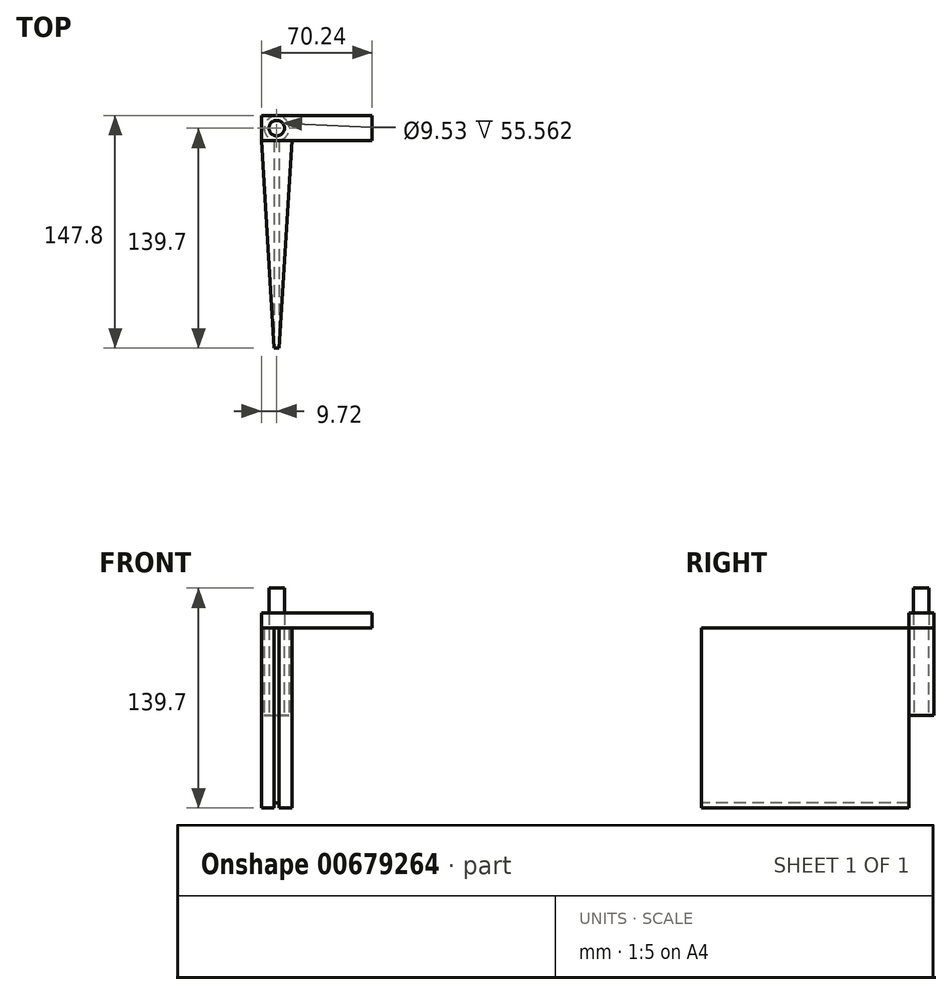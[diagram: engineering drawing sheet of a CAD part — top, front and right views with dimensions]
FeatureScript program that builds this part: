
annotation { "Feature Type Name" : "Feature", "Feature Type Description" : "" }
export const myFeature = defineFeature(function(context is Context, id is Id, definition is map)
    precondition{}
    {
        {
            var Q0;
            Q0=qCreatedBy(makeId("Top.planeOp"),FACE);
            var sketch = newSketch(context, id + "F0", { "sketchPlane" : qUnion([Q0])});
            skCircle(sketch, "E0", {"center": v(0, 0) * mm, "radius": 7.94 * mm});
            skCircle(sketch, "E1", {"center": v(0, 0) * mm, "radius": 4.76 * mm});
            skLineSegment(sketch, "E2.top", {"start": v(1.59, -139.7) * mm, "end": v(-1.59, -139.7) * mm});
            skLineSegment(sketch, "E2.left", {"start": v(1.59, 0) * mm, "end": v(1.59, -139.7) * mm});
            skLineSegment(sketch, "E2.right", {"start": v(-1.59, 0) * mm, "end": v(-1.59, -139.7) * mm});
            skLineSegment(sketch, "E3", {"start": v(-4.76, 0) * mm, "end": v(4.76, 0) * mm});
            skPoint(sketch, "E2.bottom.end.orphan", {"position": v(-1.59, 139.7) * mm});
            skPoint(sketch, "E2.bottom.start.orphan", {"position": v(1.59, 139.7) * mm});
            skSolve(sketch);
        }
        {
            var Q0;
            Q0=qSketchRegion(id+"F0",true);
            extrude(context, id + "F1", {"entities" : qUnion([Q0]), "depth" : 55.56 * mm});
        }
        {
            var Q0;
            Q0=makeQuery(id+"F1.opExtrude","CAP_FACE",FACE,{"disambiguationData":[OSD([sQuery(id+"F0.wireOp",EDGE,"E0"),sQuery(id+"F0.wireOp",EDGE,"E1"),sQuery(id+"F0.wireOp",EDGE,"E2.top"),sQuery(id+"F0.wireOp",EDGE,"E2.left"),sQuery(id+"F0.wireOp",EDGE,"E2.right")])],"isStart":true});
            var sketch = newSketch(context, id + "F2", { "sketchPlane" : qUnion([Q0])});
            skLineSegment(sketch, "E4.bottom", {"start": v(-1.59, 7.78) * mm, "end": v(1.59, 7.78) * mm});
            skLineSegment(sketch, "E4.top", {"start": v(-1.59, 139.7) * mm, "end": v(1.59, 139.7) * mm});
            skLineSegment(sketch, "E4.left", {"start": v(-1.59, 7.78) * mm, "end": v(-1.59, 139.7) * mm});
            skLineSegment(sketch, "E4.right", {"start": v(1.59, 7.78) * mm, "end": v(1.59, 139.7) * mm});
            skSolve(sketch);
        }
        {
            var Q0;
            Q0=qSketchRegion(id+"F2",true);
            extrude(context, id + "F3", {"entities" : qUnion([Q0]), "operationType" : NewBodyOperationType.ADD, "depth" : 55.56 * mm});
        }
        {
            var Q0;
            Q0=makeQuery(id+"F1.opExtrude","CAP_FACE",FACE,{"disambiguationData":[OSD([sQuery(id+"F0.wireOp",EDGE,"E0"),sQuery(id+"F0.wireOp",EDGE,"E1"),sQuery(id+"F0.wireOp",EDGE,"E2.top"),sQuery(id+"F0.wireOp",EDGE,"E2.left"),sQuery(id+"F0.wireOp",EDGE,"E2.right")])],"isStart":false});
            var sketch = newSketch(context, id + "F4", { "sketchPlane" : qUnion([Q0])});
            skLineSegment(sketch, "E5", {"start": v(-1.59, -7.78) * mm, "end": v(-9.72, -7.78) * mm});
            skLineSegment(sketch, "E6", {"start": v(1.59, -7.78) * mm, "end": v(9.72, -7.78) * mm});
            skLineSegment(sketch, "E7", {"start": v(-9.72, -7.78) * mm, "end": v(-1.59, -139.7) * mm});
            skLineSegment(sketch, "E8", {"start": v(-1.59, -139.7) * mm, "end": v(-1.59, -7.78) * mm});
            skLineSegment(sketch, "E9", {"start": v(9.72, -7.78) * mm, "end": v(1.59, -139.7) * mm});
            skLineSegment(sketch, "E10", {"start": v(1.59, -139.7) * mm, "end": v(1.59, -7.78) * mm});
            skSolve(sketch);
        }
        {
            var Q0;
            Q0=qSketchRegion(id+"F4",true);
            extrude(context, id + "F5", {"entities" : qUnion([Q0]), "operationType" : NewBodyOperationType.ADD, "oppositeDirection" : true, "depth" : 114.3 * mm});
        }
        {
            var Q0;
            Q0=makeQuery(id+"F5.boolean.opBoolean","MERGE",FACE,{"derivedFrom":[makeQuery(id+"F1.opExtrude","CAP_FACE",FACE,{"disambiguationData":[OSD([sQuery(id+"F0.wireOp",EDGE,"E0"),sQuery(id+"F0.wireOp",EDGE,"E1"),sQuery(id+"F0.wireOp",EDGE,"E2.top"),sQuery(id+"F0.wireOp",EDGE,"E2.left"),sQuery(id+"F0.wireOp",EDGE,"E2.right")])],"isStart":false}),makeQuery(id+"F5.opExtrude","CAP_FACE",FACE,{"disambiguationData":[OSD([sQuery(id+"F4.wireOp",EDGE,"E5"),sQuery(id+"F4.wireOp",EDGE,"E7"),sQuery(id+"F4.wireOp",EDGE,"E8")])],"isStart":true}),makeQuery(id+"F5.opExtrude","CAP_FACE",FACE,{"disambiguationData":[OSD([sQuery(id+"F4.wireOp",EDGE,"E6"),sQuery(id+"F4.wireOp",EDGE,"E9"),sQuery(id+"F4.wireOp",EDGE,"E10")])],"isStart":true})]});
            var sketch = newSketch(context, id + "F6", { "sketchPlane" : qUnion([Q0])});
            skCircle(sketch, "E11", {"center": v(0, 0) * mm, "radius": 4.93 * mm});
            skSolve(sketch);
        }
        {
            var Q0;
            Q0=qSketchRegion(id+"F6",true);
            extrude(context, id + "F7", {"entities" : qUnion([Q0]), "operationType" : NewBodyOperationType.ADD, "depth" : 25.4 * mm});
        }
        {
            var Q0;
            Q0=makeQuery(id+"F5.boolean.opBoolean","MERGE",FACE,{"derivedFrom":[makeQuery(id+"F1.opExtrude","CAP_FACE",FACE,{"disambiguationData":[OSD([sQuery(id+"F0.wireOp",EDGE,"E0"),sQuery(id+"F0.wireOp",EDGE,"E1"),sQuery(id+"F0.wireOp",EDGE,"E2.top"),sQuery(id+"F0.wireOp",EDGE,"E2.left"),sQuery(id+"F0.wireOp",EDGE,"E2.right")])],"isStart":false}),makeQuery(id+"F5.opExtrude","CAP_FACE",FACE,{"disambiguationData":[OSD([sQuery(id+"F4.wireOp",EDGE,"E5"),sQuery(id+"F4.wireOp",EDGE,"E7"),sQuery(id+"F4.wireOp",EDGE,"E8")])],"isStart":true}),makeQuery(id+"F5.opExtrude","CAP_FACE",FACE,{"disambiguationData":[OSD([sQuery(id+"F4.wireOp",EDGE,"E6"),sQuery(id+"F4.wireOp",EDGE,"E9"),sQuery(id+"F4.wireOp",EDGE,"E10")])],"isStart":true})]});
            var sketch = newSketch(context, id + "F8", { "sketchPlane" : qUnion([Q0])});
            skLineSegment(sketch, "E12.bottom", {"start": v(-9.72, -7.78) * mm, "end": v(9.72, -7.78) * mm});
            skLineSegment(sketch, "E12.top", {"start": v(-9.72, 8.1) * mm, "end": v(9.72, 8.1) * mm});
            skLineSegment(sketch, "E12.left", {"start": v(-9.72, -7.78) * mm, "end": v(-9.72, 8.1) * mm});
            skLineSegment(sketch, "E13.bottom", {"start": v(9.72, 8.1) * mm, "end": v(60.52, 8.1) * mm});
            skLineSegment(sketch, "E13.top", {"start": v(9.72, -7.78) * mm, "end": v(60.52, -7.78) * mm});
            skLineSegment(sketch, "E13.right", {"start": v(60.52, 8.1) * mm, "end": v(60.52, -7.78) * mm});
            skSolve(sketch);
        }
        {
            var Q0;
            Q0=qSketchRegion(id+"F8",true);
            extrude(context, id + "F9", {"entities" : qUnion([Q0]), "depth" : 9.52 * mm});
        }
    });
